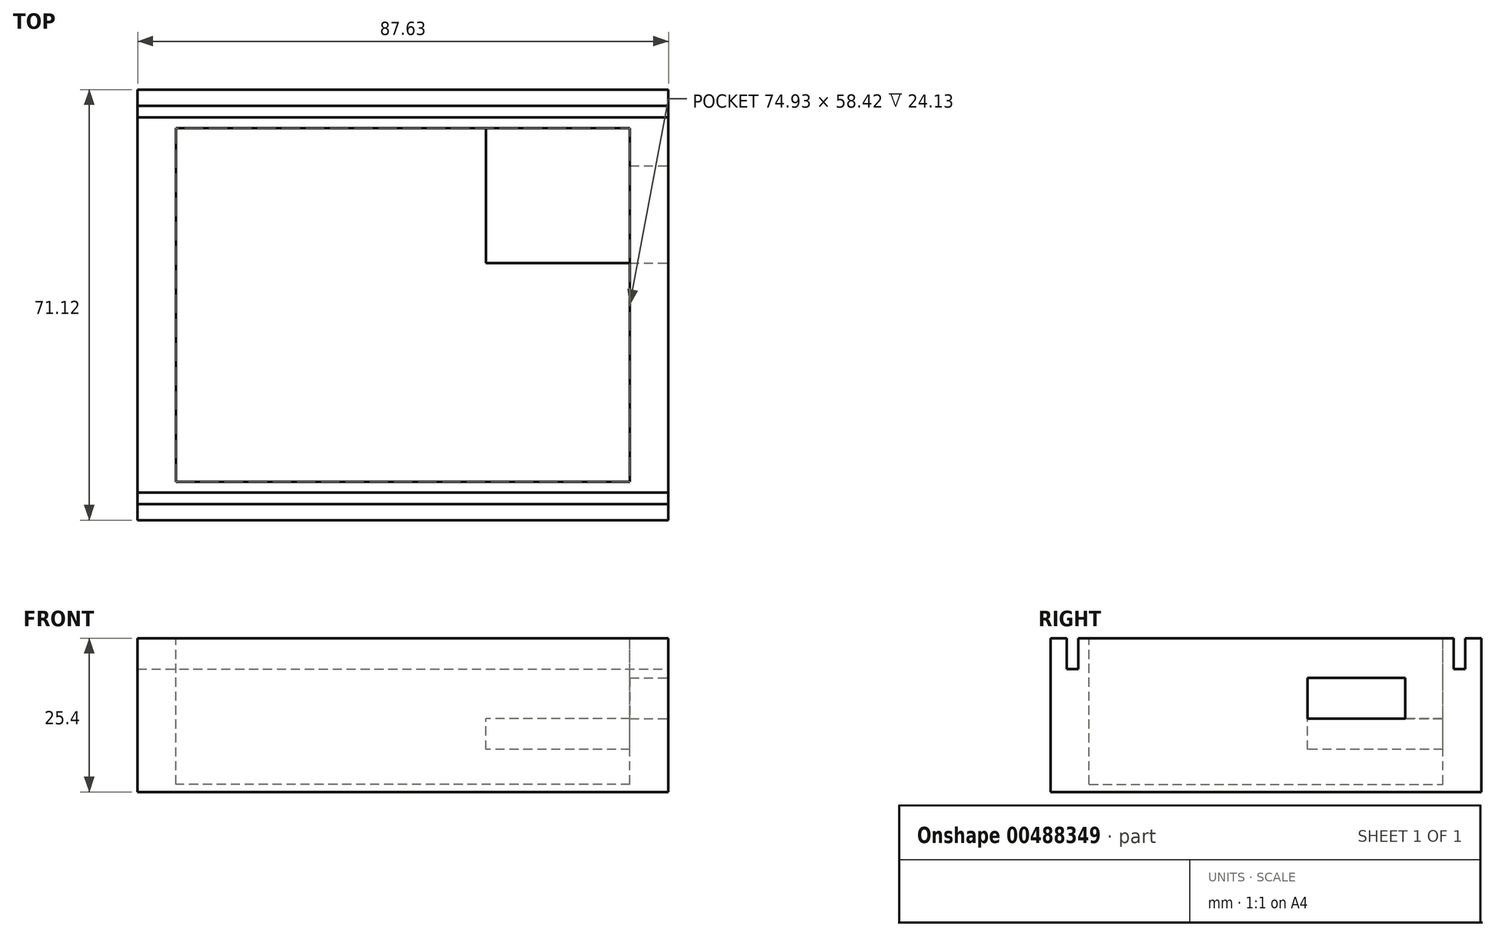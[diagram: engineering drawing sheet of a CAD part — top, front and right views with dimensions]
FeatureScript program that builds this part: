
annotation { "Feature Type Name" : "Feature", "Feature Type Description" : "" }
export const myFeature = defineFeature(function(context is Context, id is Id, definition is map)
    precondition{}
    {
        {
            var Q0;
            Q0=qCreatedBy(makeId("Top.planeOp"),FACE);
            var sketch = newSketch(context, id + "F0", { "sketchPlane" : qUnion([Q0])});
            skLineSegment(sketch, "E0.bottom", {"start": v(42.76, -42.44) * mm, "end": v(-44.87, -42.44) * mm});
            skLineSegment(sketch, "E0.top", {"start": v(42.76, 28.68) * mm, "end": v(-44.87, 28.68) * mm});
            skLineSegment(sketch, "E0.left", {"start": v(42.76, -42.44) * mm, "end": v(42.76, 28.68) * mm});
            skLineSegment(sketch, "E0.right", {"start": v(-44.87, -42.44) * mm, "end": v(-44.87, 28.68) * mm});
            skSolve(sketch);
        }
        {
            var Q0;
            Q0=makeQuery(id+"F0.imprint","IMPRINT",FACE,{"disambiguationData":[TD([[makeQuery(id+"F0.imprint","IMPRINT",EDGE,{"derivedFrom":sQuery(id+"F0.wireOp",EDGE,"E0.bottom")}),-1.0]])]});
            var Q1;
            Q1=sQuery(id+"F0.wireOp",EDGE,"E0.right");
            var Q2;
            Q2=sQuery(id+"F0.wireOp",EDGE,"E0.bottom");
            var Q3;
            Q3=sQuery(id+"F0.wireOp",EDGE,"E0.top");
            var Q4;
            Q4=sQuery(id+"F0.wireOp",EDGE,"E0.left");
            extrude(context, id + "F1", {"entities" : qUnion([Q0]), "surfaceEntities" : qUnion([Q1, Q2, Q3, Q4]), "depth" : 25.4 * mm, "offsetDistance" : 25.4 * mm});
        }
        {
            var Q0;
            Q0=makeQuery(id+"F1.opExtrude","CAP_FACE",FACE,{"disambiguationData":[OSD([sQuery(id+"F0.wireOp",EDGE,"E0.bottom"),sQuery(id+"F0.wireOp",EDGE,"E0.top"),sQuery(id+"F0.wireOp",EDGE,"E0.left"),sQuery(id+"F0.wireOp",EDGE,"E0.right")])],"isStart":false});
            var sketch = newSketch(context, id + "F2", { "sketchPlane" : qUnion([Q0])});
            skPoint(sketch, "E1.middle", {"position": v(0, 0) * mm});
            skLineSegment(sketch, "E2.0", {"start": v(-38.52, -36.09) * mm, "end": v(-38.52, 22.33) * mm});
            skLineSegment(sketch, "E3.0", {"start": v(36.4, 22.33) * mm, "end": v(-38.52, 22.33) * mm});
            skLineSegment(sketch, "E4.0", {"start": v(36.4, -36.09) * mm, "end": v(36.4, 22.33) * mm});
            skLineSegment(sketch, "E5.0", {"start": v(36.4, -36.09) * mm, "end": v(-38.52, -36.09) * mm});
            skSolve(sketch);
        }
        {
            var Q0;
            Q0=makeQuery(id+"F2.imprint","IMPRINT",FACE,{"disambiguationData":[TD([[makeQuery(id+"F2.imprint","IMPRINT",EDGE,{"derivedFrom":sQuery(id+"F2.wireOp",EDGE,"E2.0")}),-1.0]])]});
            extrude(context, id + "F3", {"entities" : qUnion([Q0]), "operationType" : NewBodyOperationType.REMOVE, "oppositeDirection" : true, "depth" : 24.13 * mm, "offsetDistance" : 25.4 * mm});
        }
        {
            var Q0;
            Q0=makeQuery(id+"F1.opExtrude","SWEPT_FACE",FACE,{"disambiguationData":[OSD([sQuery(id+"F0.wireOp",EDGE,"E0.left")])]});
            var sketch = newSketch(context, id + "F4", { "sketchPlane" : qUnion([Q0])});
            skLineSegment(sketch, "E6", {"start": v(0, 0) * mm, "end": v(0, 25.4) * mm});
            skLineSegment(sketch, "E7", {"start": v(0, 25.4) * mm, "end": v(0, 18.85) * mm});
            skLineSegment(sketch, "E8", {"start": v(0, 18.85) * mm, "end": v(16.08, 18.85) * mm});
            skLineSegment(sketch, "E9", {"start": v(16.08, 18.85) * mm, "end": v(16.08, 12.09) * mm});
            skLineSegment(sketch, "E10", {"start": v(16.08, 12.09) * mm, "end": v(0, 12.09) * mm});
            skLineSegment(sketch, "E11", {"start": v(0, 12.09) * mm, "end": v(0, 18.85) * mm});
            skSolve(sketch);
        }
        {
            var Q0;
            Q0=makeQuery(id+"F4.imprint","IMPRINT",FACE,{"disambiguationData":[TD([[makeQuery(id+"F4.imprint","IMPRINT",EDGE,{"derivedFrom":sQuery(id+"F4.wireOp",EDGE,"E8")}),-1.0]])]});
            extrude(context, id + "F5", {"entities" : qUnion([Q0]), "operationType" : NewBodyOperationType.REMOVE, "oppositeDirection" : true, "depth" : 7.62 * mm, "offsetDistance" : 25.4 * mm});
        }
        {
            var Q0;
            Q0=makeQuery(id+"F1.opExtrude","CAP_FACE",FACE,{"disambiguationData":[OSD([sQuery(id+"F0.wireOp",EDGE,"E0.bottom"),sQuery(id+"F0.wireOp",EDGE,"E0.top"),sQuery(id+"F0.wireOp",EDGE,"E0.left"),sQuery(id+"F0.wireOp",EDGE,"E0.right")])],"isStart":false});
            var sketch = newSketch(context, id + "F6", { "sketchPlane" : qUnion([Q0])});
            skLineSegment(sketch, "E12", {"start": v(-44.87, 28.68) * mm, "end": v(-44.87, 26.01) * mm});
            skLineSegment(sketch, "E13", {"start": v(-44.87, 26.01) * mm, "end": v(-44.87, 24.1) * mm});
            skLineSegment(sketch, "E14", {"start": v(-44.87, 24.1) * mm, "end": v(42.76, 24.1) * mm});
            skLineSegment(sketch, "E15", {"start": v(42.76, 24.1) * mm, "end": v(42.76, 26.01) * mm});
            skLineSegment(sketch, "E16", {"start": v(42.76, 26.01) * mm, "end": v(-44.87, 26.01) * mm});
            skLineSegment(sketch, "E17", {"start": v(-44.87, -42.44) * mm, "end": v(-44.87, -39.77) * mm});
            skLineSegment(sketch, "E18", {"start": v(-44.87, -39.77) * mm, "end": v(-44.87, -37.87) * mm});
            skLineSegment(sketch, "E19", {"start": v(-44.87, -37.87) * mm, "end": v(42.76, -37.87) * mm});
            skLineSegment(sketch, "E20", {"start": v(42.76, -37.87) * mm, "end": v(42.76, -39.77) * mm});
            skLineSegment(sketch, "E21", {"start": v(42.76, -39.77) * mm, "end": v(-44.87, -39.77) * mm});
            skSolve(sketch);
        }
        {
            var Q0;
            Q0=makeQuery(id+"F6.imprint","IMPRINT",FACE,{"disambiguationData":[TD([[makeQuery(id+"F6.imprint","IMPRINT",EDGE,{"derivedFrom":sQuery(id+"F6.wireOp",EDGE,"E13")}),-1.0]])]});
            var Q1;
            Q1=makeQuery(id+"F6.imprint","IMPRINT",FACE,{"disambiguationData":[TD([[makeQuery(id+"F6.imprint","IMPRINT",EDGE,{"derivedFrom":sQuery(id+"F6.wireOp",EDGE,"E18")}),-1.0]])]});
            extrude(context, id + "F7", {"entities" : qUnion([Q0, Q1]), "operationType" : NewBodyOperationType.REMOVE, "oppositeDirection" : true, "depth" : 5.08 * mm, "offsetDistance" : 25.4 * mm});
        }
        {
            var Q0;
            Q0=makeQuery(id+"F5.boolean.opBoolean","COPY",FACE,{"derivedFrom":makeQuery(id+"F5.opExtrude","SWEPT_FACE",FACE,{"disambiguationData":[OSD([sQuery(id+"F4.wireOp",EDGE,"E10")])]})});
            var sketch = newSketch(context, id + "F8", { "sketchPlane" : qUnion([Q0])});
            skLineSegment(sketch, "E22.bottom", {"start": v(36.4, 0) * mm, "end": v(12.6, 0) * mm});
            skLineSegment(sketch, "E22.top", {"start": v(36.4, 22.33) * mm, "end": v(12.6, 22.33) * mm});
            skLineSegment(sketch, "E22.left", {"start": v(36.4, 0) * mm, "end": v(36.4, 22.33) * mm});
            skLineSegment(sketch, "E22.right", {"start": v(12.6, 0) * mm, "end": v(12.6, 22.33) * mm});
            skSolve(sketch);
        }
        {
            var Q0;
            {var subQ4=sQuery(id+"F8.wireOp",EDGE,"E22.bottom");Q0=makeQuery(id+"F8.imprint","IMPRINT",FACE,{"disambiguationData":[TD([[makeQuery(id+"F8.imprint","IMPRINT",EDGE,{"derivedFrom":subQ4}),-1.0]])]});}
            extrude(context, id + "F9", {"entities" : qUnion([Q0]), "operationType" : NewBodyOperationType.ADD, "oppositeDirection" : true, "depth" : 5.08 * mm, "offsetDistance" : 25.4 * mm});
        }
    });
